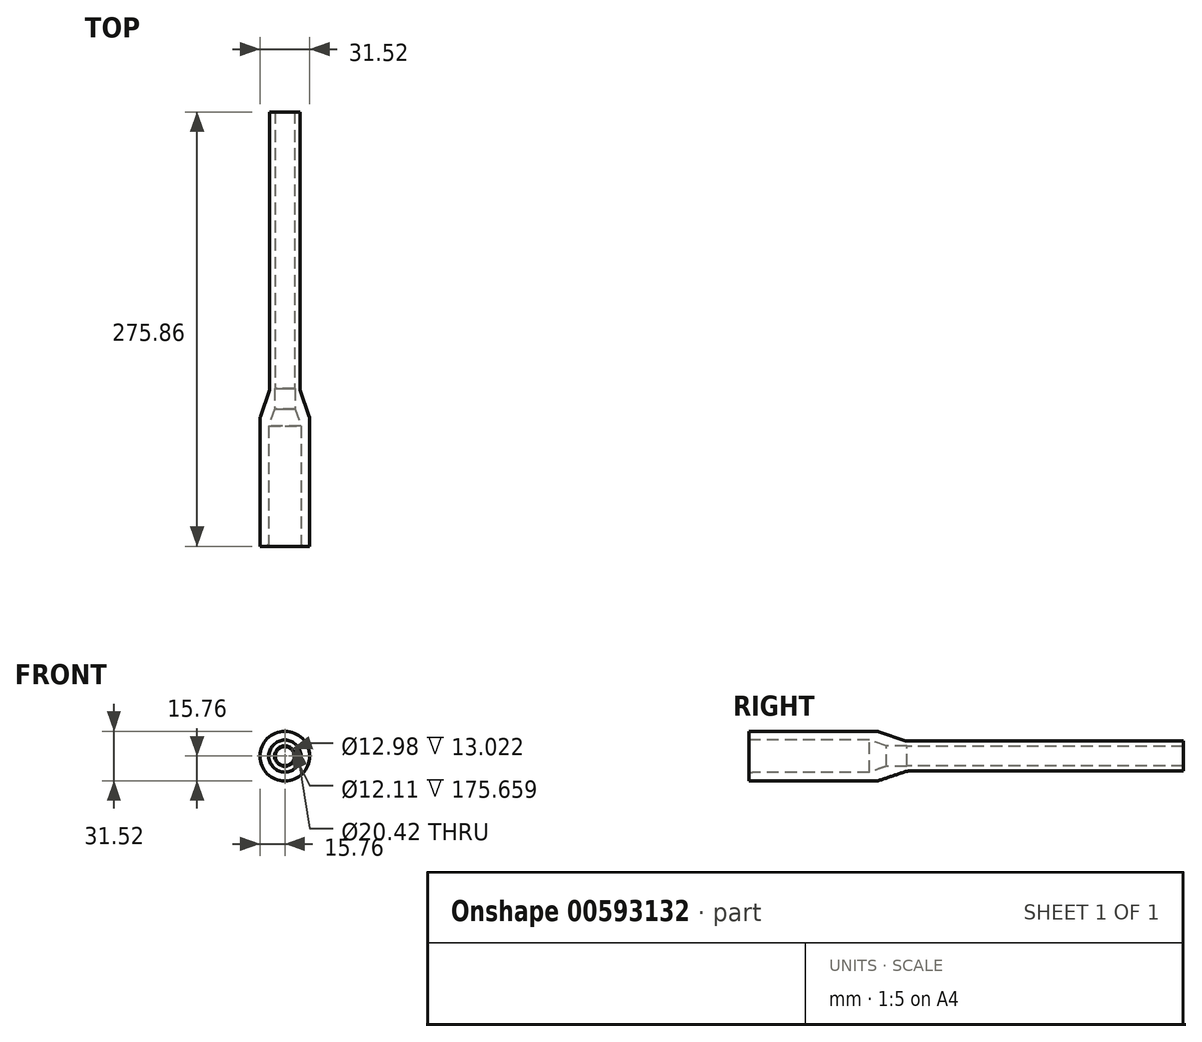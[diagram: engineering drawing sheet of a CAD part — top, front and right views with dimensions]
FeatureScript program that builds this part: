
annotation { "Feature Type Name" : "Feature", "Feature Type Description" : "" }
export const myFeature = defineFeature(function(context is Context, id is Id, definition is map)
    precondition{}
    {
        {
            var Q0;
            Q0=qCreatedBy(makeId("Right.planeOp"),FACE);
            var sketch = newSketch(context, id + "F0", { "sketchPlane" : qUnion([Q0])});
            skLineSegment(sketch, "E0", {"start": v(34.54, 55.63) * mm, "end": v(34.54, 55.63) * mm});
            skPoint(sketch, "E1.orphan", {"position": v(2.16, 0) * mm});
            skPoint(sketch, "E2.end.orphan", {"position": v(2.16, 5.1) * mm});
            skPoint(sketch, "E2.start.orphan", {"position": v(0, 5.1) * mm});
            skPoint(sketch, "E3.orphan", {"position": v(75.43, 0) * mm});
            skPoint(sketch, "E4.end.orphan", {"position": v(76.35, 0) * mm});
            skLineSegment(sketch, "E5", {"start": v(0, 22.27) * mm, "end": v(100.2, 22.27) * mm, "construction": true});
            skLineSegment(sketch, "E6", {"start": v(100.2, 6.49) * mm, "end": v(87.18, 6.49) * mm});
            skLineSegment(sketch, "E7", {"start": v(87.18, 6.49) * mm, "end": v(76.35, 10.21) * mm});
            skPoint(sketch, "E8.start.orphan", {"position": v(87.18, 0) * mm});
            skLineSegment(sketch, "E9", {"start": v(100.2, 6.49) * mm, "end": v(100.2, 6.06) * mm});
            skLineSegment(sketch, "E10.trimOffspring", {"start": v(6.67, 10.21) * mm, "end": v(76.35, 10.21) * mm});
            skPoint(sketch, "E11.visualSharp", {"position": v(6.67, 9.78) * mm});
            skPoint(sketch, "E12.end.orphan", {"position": v(76.35, 9.78) * mm});
            skPoint(sketch, "E13.end.orphan", {"position": v(87.18, 6.06) * mm});
            skPoint(sketch, "E14.start.orphan", {"position": v(4.41, 1.46) * mm});
            skPoint(sketch, "E15.start.orphan", {"position": v(4.41, 4.02) * mm});
            skPoint(sketch, "E16.start.orphan", {"position": v(0, 4.02) * mm});
            skPoint(sketch, "E17.start.orphan", {"position": v(0, 10.21) * mm});
            skPoint(sketch, "E18.start.orphan", {"position": v(0, 0) * mm});
            skLineSegment(sketch, "E19", {"start": v(6.67, 10.21) * mm, "end": v(0, 10.21) * mm});
            skLineSegment(sketch, "E20", {"start": v(0, 10.21) * mm, "end": v(0, 15.76) * mm});
            skLineSegment(sketch, "E21", {"start": v(0, 15.76) * mm, "end": v(81.77, 15.76) * mm});
            skPoint(sketch, "E21.endSnap0", {"position": v(81.77, 8.35) * mm});
            skLineSegment(sketch, "E22", {"start": v(81.77, 15.76) * mm, "end": v(100.2, 9.54) * mm});
            skLineSegment(sketch, "E23", {"start": v(100.2, 9.54) * mm, "end": v(181.67, 9.54) * mm});
            skLineSegment(sketch, "E24", {"start": v(100.2, 6.06) * mm, "end": v(181.67, 6.06) * mm});
            skLineSegment(sketch, "E25", {"start": v(181.67, 6.06) * mm, "end": v(181.67, 9.54) * mm});
            skLineSegment(sketch, "E26", {"start": v(0, 0) * mm, "end": v(7.05, 0) * mm, "construction": true});
            skSolve(sketch);
        }
        {
            var Q0;
            Q0=makeQuery(id+"F0.imprint","IMPRINT",FACE,{"disambiguationData":[TD([[makeQuery(id+"F0.imprint","IMPRINT",EDGE,{"derivedFrom":sQuery(id+"F0.wireOp",EDGE,"E6")}),-1.0]])]});
            var Q1;
            Q1=sQuery(id+"F0.wireOp",EDGE,"E26");
            revolve(context, id + "F1", {"entities" : qUnion([Q0]), "axis" : qUnion([Q1]), "revolveType" : RevolveType.FULL});
        }
        {
            var Q0;
            Q0=makeQuery(id+"F1.opRevolve","SWEPT_EDGE",EDGE,{"disambiguationData":[OSD([sQuery(id+"F0.wireOp",EDGE,"E19"),sQuery(id+"F0.wireOp",EDGE,"E20")])]});
            fillet(context, id + "F2", {"entities" : qUnion([Q0]), "radius" : 2.23 * mm, "allowEdgeOverflow" : false});
        }
        {
            var Q0;
            Q0=makeQuery(id+"F1.opRevolve","SWEPT_FACE",FACE,{"disambiguationData":[OSD([sQuery(id+"F0.wireOp",EDGE,"E25")])]});
            extrude(context, id + "F3", {"entities" : qUnion([Q0]), "operationType" : NewBodyOperationType.ADD, "depth" : 94.2 * mm, "offsetDistance" : 25.4 * mm});
        }
        {
            var Q0;
            Q0=makeQuery(id+"F1.opRevolve","SWEPT_EDGE",EDGE,{"disambiguationData":[OSD([sQuery(id+"F0.wireOp",EDGE,"E21"),sQuery(id+"F0.wireOp",EDGE,"E22")])]});
            var Q1;
            Q1=makeQuery(id+"F1.opRevolve","SWEPT_EDGE",EDGE,{"disambiguationData":[OSD([sQuery(id+"F0.wireOp",EDGE,"E22"),sQuery(id+"F0.wireOp",EDGE,"E23")])]});
            fillet(context, id + "F4", {"entities" : qUnion([Q0, Q1]), "radius" : 5.08 * mm, "tangentPropagation" : true, "allowEdgeOverflow" : false});
        }
    });
